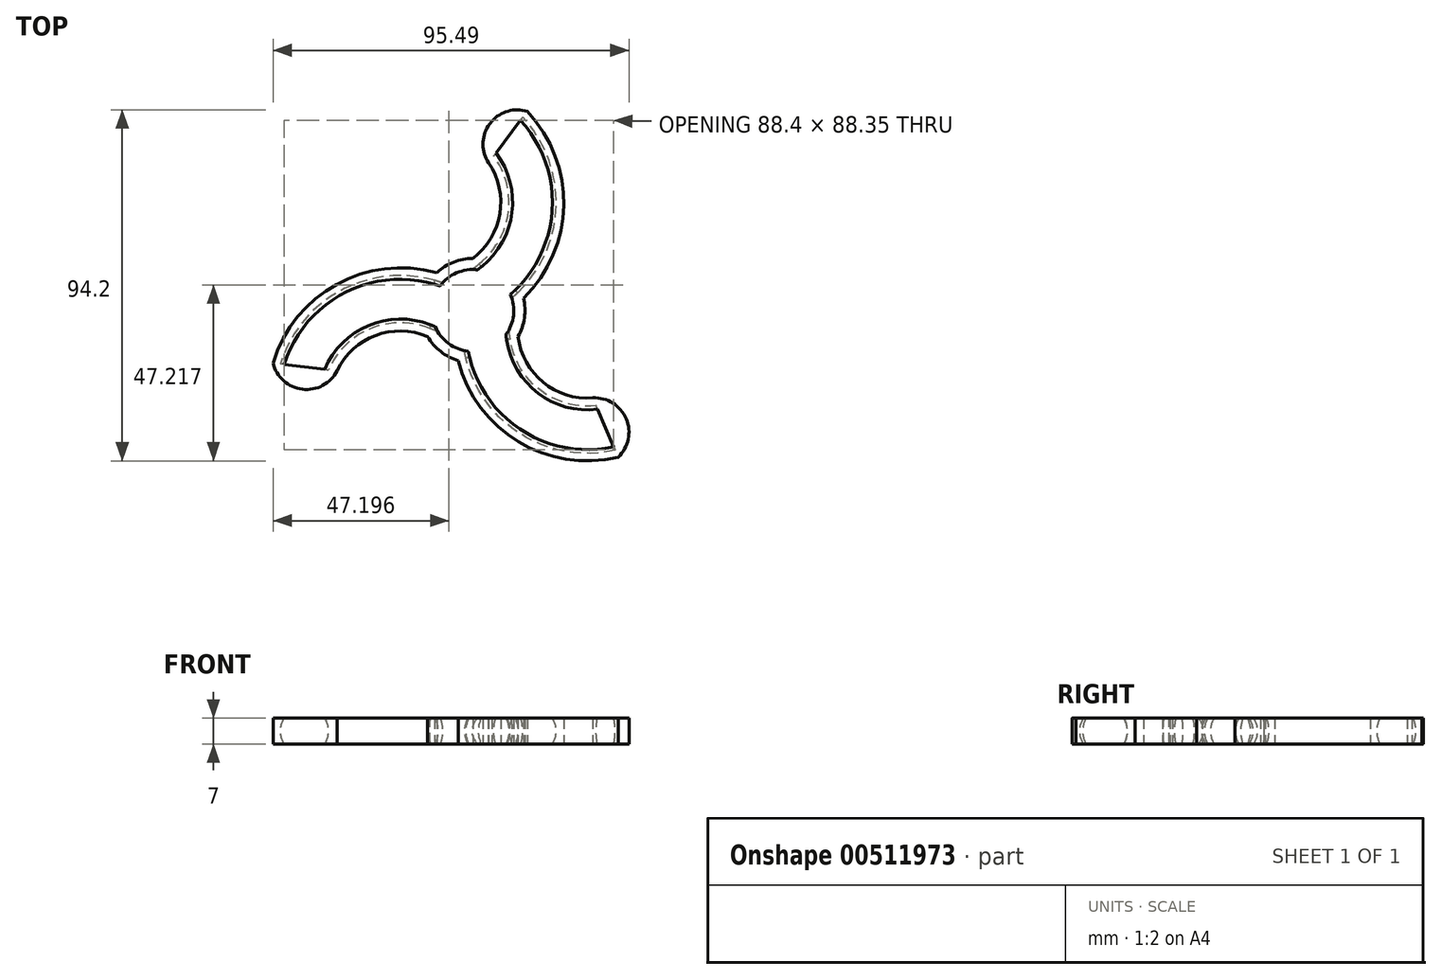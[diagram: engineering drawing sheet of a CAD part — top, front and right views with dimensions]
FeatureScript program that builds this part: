
annotation { "Feature Type Name" : "Feature", "Feature Type Description" : "" }
export const myFeature = defineFeature(function(context is Context, id is Id, definition is map)
    precondition{}
    {
        {
            var Q0;
            Q0=qCreatedBy(makeId("Top.planeOp"),FACE);
            var sketch = newSketch(context, id + "F0", { "sketchPlane" : qUnion([Q0])});
            skCircle(sketch, "E0", {"center": v(0, 0) * mm, "radius": 11 * mm});
            skCircle(sketch, "E1.0", {"center": v(0, 0) * mm, "radius": 14 * mm});
            skPoint(sketch, "E2", {"position": v(7.5, 29) * mm});
            skArc(sketch, "E3", {"start": v(0, 14) * mm, "mid": v(7.25, 25.96) * mm, "end": v(4.2, 39.61) * mm});
            skArc(sketch, "E4.trimOffspring", {"start": v(13.6, 3.3) * mm, "mid": v(24.37, 28.18) * mm, "end": v(14.6, 53.46) * mm});
            skArc(sketch, "E5.0", {"start": v(6.84, 8.62) * mm, "mid": v(15.93, 27.1) * mm, "end": v(9.5, 46.66) * mm});
            skLineSegment(sketch, "E6", {"start": v(5.1, 50.8) * mm, "end": v(4.1, 49.47) * mm});
            skArc(sketch, "E7", {"start": v(14.6, 53.46) * mm, "mid": v(4.57, 50.16) * mm, "end": v(4.2, 39.61) * mm});
            skPoint(sketch, "E8", {"position": v(9.5, 46.66) * mm});
            skArc(sketch, "E9.1.0", {"start": v(-9.66, 10.13) * mm, "mid": v(-36.6, 7.02) * mm, "end": v(-53.6, -14.1) * mm});
            skArc(sketch, "E9.1.1", {"start": v(-53.6, -14.1) * mm, "mid": v(-45.72, -21.12) * mm, "end": v(-36.4, -16.16) * mm});
            skArc(sketch, "E9.1.2", {"start": v(-10.88, 1.61) * mm, "mid": v(-31.43, 0.25) * mm, "end": v(-45.16, -15.1) * mm});
            skArc(sketch, "E9.1.3", {"start": v(-12.12, -7) * mm, "mid": v(-26.1, -6.7) * mm, "end": v(-36.4, -16.16) * mm});
            skArc(sketch, "E9.2.0", {"start": v(-3.94, -13.43) * mm, "mid": v(12.22, -35.2) * mm, "end": v(39, -39.37) * mm});
            skArc(sketch, "E9.2.1", {"start": v(39, -39.37) * mm, "mid": v(41.15, -29.04) * mm, "end": v(32.2, -23.45) * mm});
            skArc(sketch, "E9.2.2", {"start": v(4.04, -10.23) * mm, "mid": v(15.5, -27.35) * mm, "end": v(35.66, -31.56) * mm});
            skArc(sketch, "E9.2.3", {"start": v(12.12, -7) * mm, "mid": v(18.86, -19.26) * mm, "end": v(32.2, -23.45) * mm});
            skLineSegment(sketch, "E10", {"start": v(9.5, 46.66) * mm, "end": v(14.6, 53.46) * mm});
            skLineSegment(sketch, "E11", {"start": v(4.2, 39.61) * mm, "end": v(9.5, 46.66) * mm});
            skLineSegment(sketch, "E12.1.0", {"start": v(-45.16, -15.1) * mm, "end": v(-53.6, -14.1) * mm});
            skLineSegment(sketch, "E12.1.1", {"start": v(-36.4, -16.16) * mm, "end": v(-45.16, -15.1) * mm});
            skLineSegment(sketch, "E12.2.0", {"start": v(35.66, -31.56) * mm, "end": v(39, -39.37) * mm});
            skLineSegment(sketch, "E12.2.1", {"start": v(32.2, -23.45) * mm, "end": v(35.66, -31.56) * mm});
            skArc(sketch, "E13", {"start": v(-10.88, 1.61) * mm, "mid": v(-8.77, 0.85) * mm, "end": v(-6.7, 0) * mm});
            skArc(sketch, "E14.1.0", {"start": v(4.04, -10.23) * mm, "mid": v(3.65, -8.03) * mm, "end": v(3.35, -5.8) * mm});
            skArc(sketch, "E14.2.0", {"start": v(6.84, 8.62) * mm, "mid": v(5.13, 7.17) * mm, "end": v(3.35, 5.8) * mm});
            skSolve(sketch);
        }
        {
            var Q0;
            {var subQ0=sQuery(id+"F0.wireOp",EDGE,"E9.1.0");Q0=makeQuery(id+"F0.imprint","IMPRINT",FACE,{"disambiguationData":[TD([[makeQuery(id+"F0.imprint","IMPRINT",EDGE,{"derivedFrom":subQ0}),1.0]])]});}
            var Q1;
            {var subQ0=sQuery(id+"F0.wireOp",EDGE,"E9.1.3");Q1=makeQuery(id+"F0.imprint","IMPRINT",FACE,{"disambiguationData":[TD([[makeQuery(id+"F0.imprint","IMPRINT",EDGE,{"derivedFrom":subQ0}),-1.0]])]});}
            var Q2;
            {var subQ5=sQuery(id+"F0.wireOp",EDGE,"E9.1.2");var subQ7=sQuery(id+"F0.wireOp",EDGE,"E0");var subQ8=makeQuery(id+"F0.imprint","INTERSECT",VERTEX,{"derivedFrom":[subQ7,subQ5]});Q2=makeQuery(id+"F0.imprint","IMPRINT",FACE,{"disambiguationData":[TD([[makeQuery(id+"F0.imprint","IMPRINT",EDGE,{"disambiguationData":[TD([[subQ8,-1.0]])],"derivedFrom":subQ7}),-1.0]])]});}
            var Q3;
            {var subQ5=sQuery(id+"F0.wireOp",EDGE,"E5.0");var subQ7=sQuery(id+"F0.wireOp",EDGE,"E0");var subQ8=makeQuery(id+"F0.imprint","INTERSECT",VERTEX,{"derivedFrom":[subQ7,subQ5]});Q3=makeQuery(id+"F0.imprint","IMPRINT",FACE,{"disambiguationData":[TD([[makeQuery(id+"F0.imprint","IMPRINT",EDGE,{"disambiguationData":[TD([[subQ8,-1.0]])],"derivedFrom":subQ7}),-1.0]])]});}
            var Q4;
            {var subQ0=sQuery(id+"F0.wireOp",EDGE,"E3");Q4=makeQuery(id+"F0.imprint","IMPRINT",FACE,{"disambiguationData":[TD([[makeQuery(id+"F0.imprint","IMPRINT",EDGE,{"derivedFrom":subQ0}),-1.0]])]});}
            var Q5;
            {var subQ0=sQuery(id+"F0.wireOp",EDGE,"E4.trimOffspring");Q5=makeQuery(id+"F0.imprint","IMPRINT",FACE,{"disambiguationData":[TD([[makeQuery(id+"F0.imprint","IMPRINT",EDGE,{"derivedFrom":subQ0}),1.0]])]});}
            var Q6;
            {var subQ0=sQuery(id+"F0.wireOp",EDGE,"E9.2.3");Q6=makeQuery(id+"F0.imprint","IMPRINT",FACE,{"disambiguationData":[TD([[makeQuery(id+"F0.imprint","IMPRINT",EDGE,{"derivedFrom":subQ0}),-1.0]])]});}
            var Q7;
            {var subQ5=sQuery(id+"F0.wireOp",EDGE,"E5.0");var subQ7=sQuery(id+"F0.wireOp",EDGE,"E0");var subQ8=makeQuery(id+"F0.imprint","INTERSECT",VERTEX,{"derivedFrom":[subQ7,subQ5]});Q7=makeQuery(id+"F0.imprint","IMPRINT",FACE,{"disambiguationData":[TD([[makeQuery(id+"F0.imprint","IMPRINT",EDGE,{"disambiguationData":[TD([[subQ8,1.0]])],"derivedFrom":subQ7}),-1.0]])]});}
            var Q8;
            {var subQ0=sQuery(id+"F0.wireOp",EDGE,"E9.2.0");Q8=makeQuery(id+"F0.imprint","IMPRINT",FACE,{"disambiguationData":[TD([[makeQuery(id+"F0.imprint","IMPRINT",EDGE,{"derivedFrom":subQ0}),1.0]])]});}
            extrude(context, id + "F1", {"entities" : qUnion([Q0, Q1, Q2, Q3, Q4, Q5, Q6, Q7, Q8]), "endBound" : BoundingType.SYMMETRIC, "depth" : 7 * mm});
        }
        {
            var Q0;
            Q0=makeQuery(id+"F1.opExtrude","SWEPT_FACE",FACE,{"disambiguationData":[OSD([sQuery(id+"F0.wireOp",EDGE,"E10"),sQuery(id+"F0.wireOp",EDGE,"E11")])]});
            cPlane(context, id + "F2", {"entities" : qUnion([Q0]), "cplaneType" : CPlaneType.OFFSET, "offset" : 0 * mm, "width" : 150 * mm, "height" : 150 * mm});
        }
        {
            var Q0;
            Q0=makeQuery(id+"F1.opExtrude","SWEPT_FACE",FACE,{"disambiguationData":[OSD([sQuery(id+"F0.wireOp",EDGE,"E12.1.0"),sQuery(id+"F0.wireOp",EDGE,"E12.1.1")])]});
            cPlane(context, id + "F3", {"entities" : qUnion([Q0]), "cplaneType" : CPlaneType.OFFSET, "offset" : 0 * mm, "width" : 150 * mm, "height" : 150 * mm});
        }
        {
            var Q0;
            Q0=qCreatedBy(id+"F3.planeOp",FACE);
            var sketch = newSketch(context, id + "F4", { "sketchPlane" : qUnion([Q0])});
            skCircle(sketch, "E15", {"center": v(-43.03, 0) * mm, "radius": 6.5 * mm});
            skSolve(sketch);
        }
        {
            var Q0;
            Q0=makeQuery(id+"F4.imprint","IMPRINT",FACE,{"disambiguationData":[TD([[makeQuery(id+"F4.imprint","IMPRINT",EDGE,{"derivedFrom":sQuery(id+"F4.wireOp",EDGE,"E15")}),1.0]])]});
            var Q1;
            Q1=sQuery(id+"F0.wireOp",EDGE,"E9.1.2");
            var Q2;
            Q2=sQuery(id+"F0.wireOp",EDGE,"E13");
            sweep(context, id + "F5", {"operationType" : NewBodyOperationType.REMOVE, "profiles" : qUnion([Q0]), "path" : qUnion([Q1, Q2])});
        }
        {
            var Q0;
            Q0=qCreatedBy(id+"F2.planeOp",FACE);
            var sketch = newSketch(context, id + "F6", { "sketchPlane" : qUnion([Q0])});
            skCircle(sketch, "E16", {"center": v(-43.03, 0) * mm, "radius": 6.5 * mm});
            skSolve(sketch);
        }
        {
            var Q0;
            Q0=makeQuery(id+"F6.imprint","IMPRINT",FACE,{"disambiguationData":[TD([[makeQuery(id+"F6.imprint","IMPRINT",EDGE,{"derivedFrom":sQuery(id+"F6.wireOp",EDGE,"E16")}),1.0]])]});
            var Q1;
            Q1=sQuery(id+"F0.wireOp",EDGE,"E5.0");
            var Q2;
            Q2=sQuery(id+"F0.wireOp",EDGE,"E14.2.0");
            sweep(context, id + "F7", {"operationType" : NewBodyOperationType.REMOVE, "profiles" : qUnion([Q0]), "path" : qUnion([Q1, Q2])});
        }
        {
            var Q0;
            Q0=makeQuery(id+"F1.opExtrude","SWEPT_FACE",FACE,{"disambiguationData":[OSD([sQuery(id+"F0.wireOp",EDGE,"E12.2.0"),sQuery(id+"F0.wireOp",EDGE,"E12.2.1")])]});
            cPlane(context, id + "F8", {"entities" : qUnion([Q0]), "cplaneType" : CPlaneType.OFFSET, "offset" : 0 * mm, "width" : 150 * mm, "height" : 150 * mm});
        }
        {
            var Q0;
            Q0=qCreatedBy(id+"F8.planeOp",FACE);
            var sketch = newSketch(context, id + "F9", { "sketchPlane" : qUnion([Q0])});
            skCircle(sketch, "E17", {"center": v(-42.98, 0) * mm, "radius": 6.5 * mm});
            skSolve(sketch);
        }
        {
            var Q0;
            Q0=makeQuery(id+"F9.imprint","IMPRINT",FACE,{"disambiguationData":[TD([[makeQuery(id+"F9.imprint","IMPRINT",EDGE,{"derivedFrom":sQuery(id+"F9.wireOp",EDGE,"E17")}),1.0]])]});
            var Q1;
            Q1=sQuery(id+"F0.wireOp",EDGE,"E9.2.2");
            var Q2;
            Q2=sQuery(id+"F0.wireOp",EDGE,"E14.1.0");
            sweep(context, id + "F10", {"operationType" : NewBodyOperationType.REMOVE, "profiles" : qUnion([Q0]), "path" : qUnion([Q1, Q2])});
        }
        {
            var Q0;
            {var subQ3=sQuery(id+"F0.wireOp",EDGE,"E6");Q0=makeQuery(id+"F0.imprint","IMPRINT",FACE,{"disambiguationData":[TD([[makeQuery(id+"F0.imprint","IMPRINT",EDGE,{"derivedFrom":subQ3}),1.0]])]});}
            var Q1;
            Q1=makeQuery(id+"F0.imprint","IMPRINT",FACE,{"disambiguationData":[TD([[makeQuery(id+"F0.imprint","IMPRINT",EDGE,{"derivedFrom":sQuery(id+"F0.wireOp",EDGE,"E9.1.1")}),1.0]])]});
            var Q2;
            Q2=makeQuery(id+"F0.imprint","IMPRINT",FACE,{"disambiguationData":[TD([[makeQuery(id+"F0.imprint","IMPRINT",EDGE,{"derivedFrom":sQuery(id+"F0.wireOp",EDGE,"E9.2.1")}),1.0]])]});
            extrude(context, id + "F11", {"entities" : qUnion([Q0, Q1, Q2]), "operationType" : NewBodyOperationType.ADD, "endBound" : BoundingType.SYMMETRIC, "depth" : 7 * mm});
        }
    });
